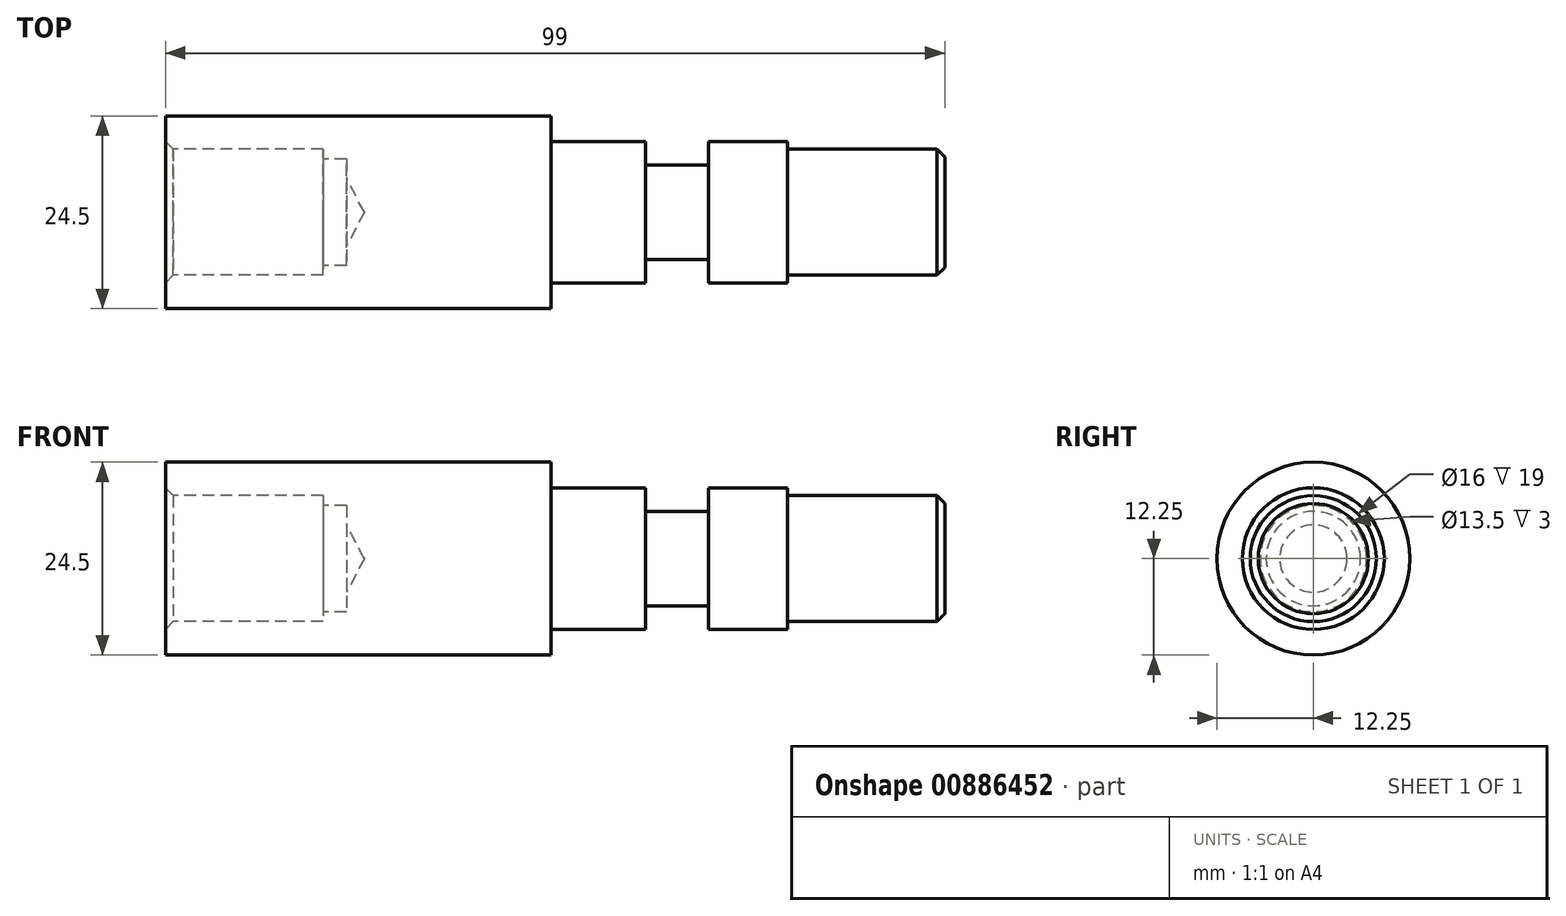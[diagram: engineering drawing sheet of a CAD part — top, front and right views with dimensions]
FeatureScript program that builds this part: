
annotation { "Feature Type Name" : "Feature", "Feature Type Description" : "" }
export const myFeature = defineFeature(function(context is Context, id is Id, definition is map)
    precondition{}
    {
        {
            var Q0;
            Q0=qCreatedBy(makeId("Front.planeOp"),FACE);
            var sketch = newSketch(context, id + "F0", { "sketchPlane" : qUnion([Q0])});
            skLineSegment(sketch, "E0", {"start": v(-29, 8) * mm, "end": v(-49, 8) * mm});
            skLineSegment(sketch, "E1", {"start": v(-49, 8) * mm, "end": v(-49, 12.25) * mm});
            skLineSegment(sketch, "E2", {"start": v(-49, 12.25) * mm, "end": v(0, 12.25) * mm});
            skLineSegment(sketch, "E3", {"start": v(0, 12.25) * mm, "end": v(0, 9) * mm});
            skLineSegment(sketch, "E4", {"start": v(0, 9) * mm, "end": v(12, 9) * mm});
            skLineSegment(sketch, "E5", {"start": v(12, 9) * mm, "end": v(12, 6) * mm});
            skLineSegment(sketch, "E6", {"start": v(12, 6) * mm, "end": v(20, 6) * mm});
            skLineSegment(sketch, "E7", {"start": v(20, 6) * mm, "end": v(20, 9) * mm});
            skLineSegment(sketch, "E8", {"start": v(20, 9) * mm, "end": v(30, 9) * mm});
            skLineSegment(sketch, "E9", {"start": v(30, 9) * mm, "end": v(30, 8) * mm});
            skLineSegment(sketch, "E10", {"start": v(50, 8) * mm, "end": v(50, 0) * mm});
            skLineSegment(sketch, "E11", {"start": v(-29, 8) * mm, "end": v(-29, 6.75) * mm});
            skLineSegment(sketch, "E12", {"start": v(-29, 6.75) * mm, "end": v(-26, 6.75) * mm});
            skLineSegment(sketch, "E13", {"start": v(30, 8) * mm, "end": v(50, 8) * mm});
            skLineSegment(sketch, "E14", {"start": v(-26, 4.28) * mm, "end": v(-26, 6.75) * mm});
            skLineSegment(sketch, "E15", {"start": v(-26, 4.28) * mm, "end": v(-23.73, 0) * mm});
            skLineSegment(sketch, "E16", {"start": v(-23.73, 0) * mm, "end": v(50, 0) * mm});
            skSolve(sketch);
        }
        {
            var Q0;
            Q0 = qSketchRegion(id + "F0", true);
            var Q1;
            Q1=sQuery(id+"F0.wireOp",EDGE,"E16");
            revolve(context, id + "F1", {"surfaceOperationType" : NewSurfaceOperationType.NEW, "entities" : qUnion([Q0]), "axis" : qUnion([Q1]), "revolveType" : RevolveType.FULL});
        }
        {
            var Q0;
            Q0=makeQuery(id+"F1.opRevolve","SWEPT_EDGE",EDGE,{"disambiguationData":[OSD([sQuery(id+"F0.wireOp",EDGE,"E10"),sQuery(id+"F0.wireOp",EDGE,"E13")])]});
            chamfer(context, id + "F2", {"entities" : qUnion([Q0]), "width" : 1 * mm, "tangentPropagation" : true});
        }
        {
            var Q0;
            Q0=makeQuery(id+"F1.opRevolve","SWEPT_EDGE",EDGE,{"disambiguationData":[OSD([sQuery(id+"F0.wireOp",EDGE,"E0"),sQuery(id+"F0.wireOp",EDGE,"E1")])]});
            chamfer(context, id + "F3", {"entities" : qUnion([Q0]), "width" : 1 * mm, "tangentPropagation" : true});
        }
    });
